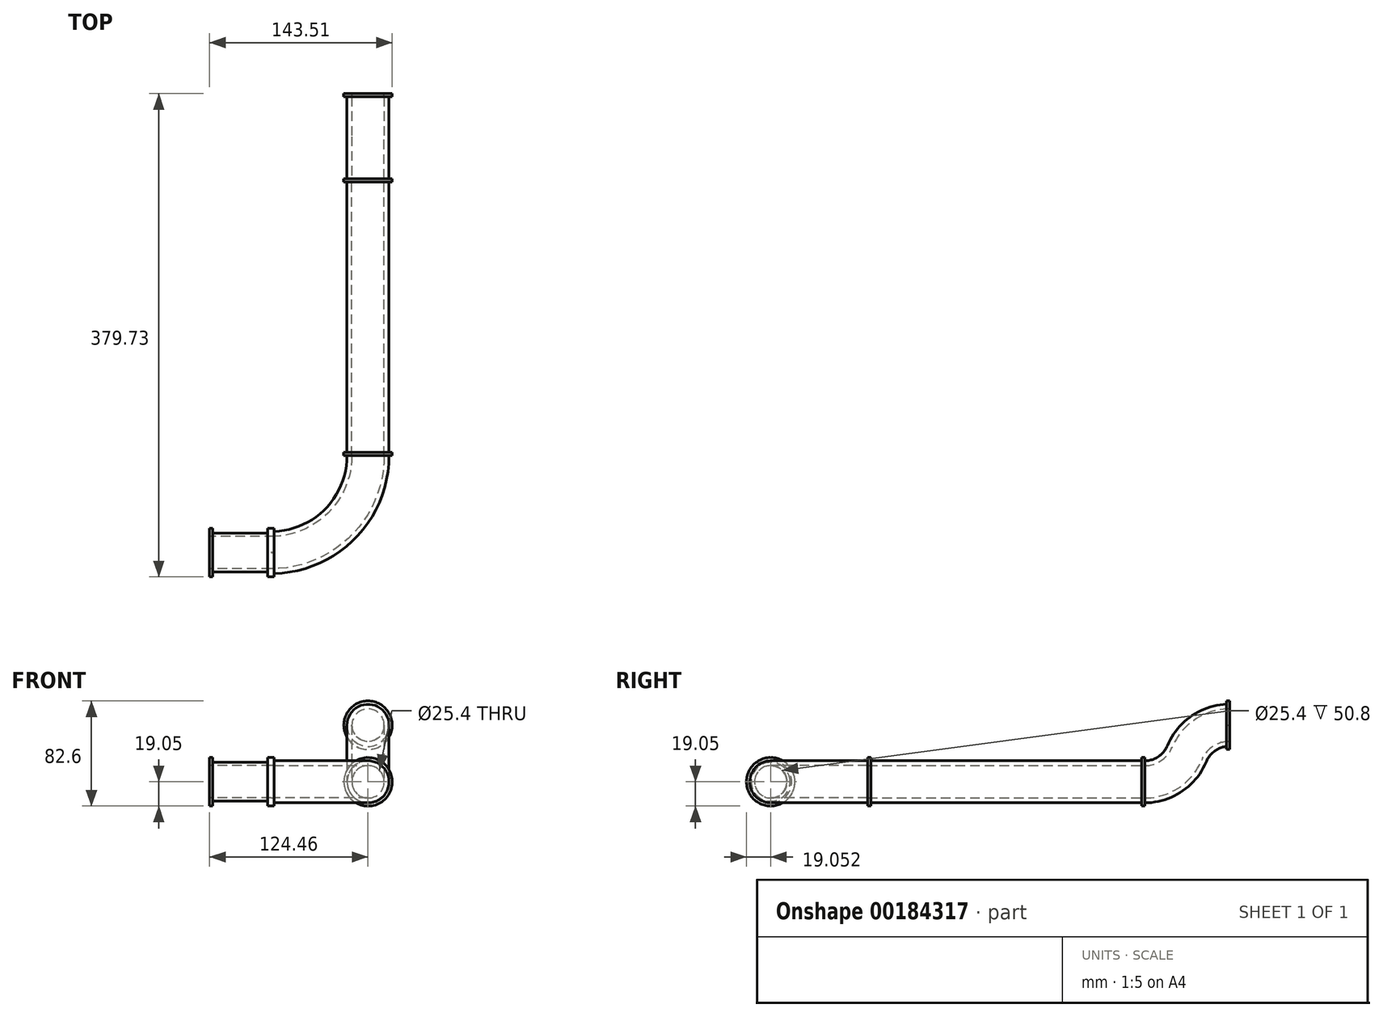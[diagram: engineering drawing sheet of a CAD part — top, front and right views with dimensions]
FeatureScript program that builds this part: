
annotation { "Feature Type Name" : "Feature", "Feature Type Description" : "" }
export const myFeature = defineFeature(function(context is Context, id is Id, definition is map)
    precondition{}
    {
        {
            var Q0;
            Q0=qCreatedBy(makeId("Front.planeOp"),FACE);
            var sketch = newSketch(context, id + "F0", { "sketchPlane" : qUnion([Q0])});
            skCircle(sketch, "E0", {"center": v(0, 0) * mm, "radius": 19.05 * mm});
            skCircle(sketch, "E1", {"center": v(0, 0) * mm, "radius": 12.7 * mm});
            skCircle(sketch, "E2", {"center": v(0, 0) * mm, "radius": 16.51 * mm});
            skSolve(sketch);
        }
        {
            var Q0;
            Q0=makeQuery(id+"F0.imprint","IMPRINT",FACE,{"disambiguationData":[TD([[makeQuery(id+"F0.imprint","IMPRINT",EDGE,{"derivedFrom":sQuery(id+"F0.wireOp",EDGE,"E0")}),1.0]])]});
            extrude(context, id + "F1", {"entities" : qUnion([Q0]), "depth" : 2.54 * mm});
        }
        {
            var Q0;
            Q0=makeQuery(id+"F0.imprint","IMPRINT",FACE,{"disambiguationData":[TD([[makeQuery(id+"F0.imprint","IMPRINT",EDGE,{"derivedFrom":sQuery(id+"F0.wireOp",EDGE,"E1")}),-1.0]])]});
            extrude(context, id + "F2", {"entities" : qUnion([Q0]), "operationType" : NewBodyOperationType.ADD, "depth" : 217.68 * mm});
        }
        {
            var Q0;
            Q0=makeQuery(id+"F2.opExtrude","CAP_FACE",FACE,{"disambiguationData":[OSD([sQuery(id+"F0.wireOp",EDGE,"E1"),sQuery(id+"F0.wireOp",EDGE,"E2")])],"isStart":false});
            var sketch = newSketch(context, id + "F3", { "sketchPlane" : qUnion([Q0])});
            skCircle(sketch, "E3", {"center": v(0, 0) * mm, "radius": 12.7 * mm});
            skCircle(sketch, "E4", {"center": v(0, 0) * mm, "radius": 19.05 * mm});
            skSolve(sketch);
        }
        {
            var Q0;
            Q0=makeQuery(id+"F3.imprint","IMPRINT",FACE,{"disambiguationData":[TD([[makeQuery(id+"F3.imprint","IMPRINT",EDGE,{"derivedFrom":sQuery(id+"F3.wireOp",EDGE,"E4")}),1.0]])]});
            extrude(context, id + "F4", {"entities" : qUnion([Q0]), "operationType" : NewBodyOperationType.ADD, "oppositeDirection" : true, "depth" : 2.54 * mm});
        }
        {
            var Q0;
            Q0=qCreatedBy(makeId("Right.planeOp"),FACE);
            var sketch = newSketch(context, id + "F5", { "sketchPlane" : qUnion([Q0])});
            skArc(sketch, "E5", {"start": v(0, 0) * mm, "mid": v(19.84, 6) * mm, "end": v(33.02, 22) * mm});
            skArc(sketch, "E6", {"start": v(66.8, 44.5) * mm, "mid": v(46.5, 38.35) * mm, "end": v(33.02, 22) * mm});
            skLineSegment(sketch, "E7", {"start": v(66.8, 44.5) * mm, "end": v(9.22, 44.5) * mm, "construction": true});
            skLineSegment(sketch, "E8", {"start": v(0, 0) * mm, "end": v(35.8, 0) * mm, "construction": true});
            skLineSegment(sketch, "E9", {"start": v(33.02, 22) * mm, "end": v(33.02, 44.5) * mm, "construction": true});
            skLineSegment(sketch, "E10", {"start": v(33.02, 44.5) * mm, "end": v(33.02, 0) * mm, "construction": true});
            skLineSegment(sketch, "E11", {"start": v(0, 0) * mm, "end": v(66.8, 44.5) * mm, "construction": true});
            skSolve(sketch);
        }
        {
            var Q0;
            Q0=makeQuery(id+"F0.imprint","IMPRINT",FACE,{"disambiguationData":[TD([[makeQuery(id+"F0.imprint","IMPRINT",EDGE,{"derivedFrom":sQuery(id+"F0.wireOp",EDGE,"E1")}),-1.0]])]});
            var Q1;
            Q1=sQuery(id+"F5.wireOp",EDGE,"E5");
            var Q2;
            Q2=sQuery(id+"F5.wireOp",EDGE,"E6");
            sweep(context, id + "F6", {"operationType" : NewBodyOperationType.ADD, "profiles" : qUnion([Q0]), "path" : qUnion([Q1, Q2])});
        }
        {
            var Q0;
            Q0=makeQuery(id+"F6.opSweep","CAP_FACE",FACE,{"disambiguationData":[OSD([sQuery(id+"F0.wireOp",EDGE,"E1"),sQuery(id+"F0.wireOp",EDGE,"E2"),sQuery(id+"F5.wireOp",VERTEX,"E6.start")])],"isStart":false});
            var sketch = newSketch(context, id + "F7", { "sketchPlane" : qUnion([Q0])});
            skCircle(sketch, "E12", {"center": v(0, 44.5) * mm, "radius": 19.05 * mm});
            skCircle(sketch, "E13", {"center": v(0, 44.5) * mm, "radius": 12.7 * mm});
            skSolve(sketch);
        }
        {
            var Q0;
            Q0 = qSketchRegion(id + "F7", true);
            extrude(context, id + "F8", {"entities" : qUnion([Q0]), "operationType" : NewBodyOperationType.ADD, "oppositeDirection" : true, "depth" : 2.54 * mm});
        }
        {
            var Q0;
            Q0=qCreatedBy(makeId("Top.planeOp"),FACE);
            var sketch = newSketch(context, id + "F9", { "sketchPlane" : qUnion([Q0])});
            skArc(sketch, "E14", {"start": v(-76.2, -293.88) * mm, "mid": v(-22.32, -271.56) * mm, "end": v(0, -217.68) * mm});
            skPoint(sketch, "E15.endSnap0", {"position": v(-22.32, -271.56) * mm});
            skSolve(sketch);
        }
        {
            var Q0;
            Q0=makeQuery(id+"F3.imprint","IMPRINT",FACE,{"disambiguationData":[TD([[makeQuery(id+"F3.imprint","IMPRINT",EDGE,{"derivedFrom":sQuery(id+"F3.wireOp",EDGE,"E3")}),-1.0]])]});
            var Q1;
            Q1=sQuery(id+"F9.wireOp",EDGE,"E14");
            sweep(context, id + "F10", {"operationType" : NewBodyOperationType.ADD, "profiles" : qUnion([Q0]), "path" : qUnion([Q1])});
        }
        {
            var Q0;
            Q0=makeQuery(id+"F10.opSweep","CAP_FACE",FACE,{"disambiguationData":[OSD([sQuery(id+"F0.wireOp",EDGE,"E2"),sQuery(id+"F3.wireOp",EDGE,"E3"),sQuery(id+"F9.wireOp",VERTEX,"E14.start")])],"isStart":false});
            var sketch = newSketch(context, id + "F11", { "sketchPlane" : qUnion([Q0])});
            skCircle(sketch, "E16", {"center": v(293.88, 0) * mm, "radius": 12.7 * mm});
            skCircle(sketch, "E17", {"center": v(293.88, 0) * mm, "radius": 19.05 * mm});
            skSolve(sketch);
        }
        {
            var Q0;
            Q0 = qSketchRegion(id + "F11", true);
            extrude(context, id + "F12", {"entities" : qUnion([Q0]), "operationType" : NewBodyOperationType.ADD, "oppositeDirection" : true, "depth" : 2.54 * mm});
        }
        {
            var Q0;
            Q0=makeQuery(id+"F12.boolean.opBoolean","MERGE",FACE,{"derivedFrom":[makeQuery(id+"F10.opSweep","CAP_FACE",FACE,{"disambiguationData":[OSD([sQuery(id+"F0.wireOp",EDGE,"E2"),sQuery(id+"F3.wireOp",EDGE,"E3"),sQuery(id+"F9.wireOp",VERTEX,"E14.start")])],"isStart":false}),makeQuery(id+"F12.opExtrude","CAP_FACE",FACE,{"disambiguationData":[OSD([sQuery(id+"F11.wireOp",EDGE,"E16"),sQuery(id+"F11.wireOp",EDGE,"E17")])],"isStart":true})]});
            var sketch = newSketch(context, id + "F13", { "sketchPlane" : qUnion([Q0])});
            skCircle(sketch, "E18", {"center": v(293.88, 0) * mm, "radius": 12.7 * mm});
            skCircle(sketch, "E19", {"center": v(293.88, 0) * mm, "radius": 19.05 * mm});
            skSolve(sketch);
        }
        {
            var Q0;
            Q0 = qSketchRegion(id + "F13", true);
            extrude(context, id + "F14", {"entities" : qUnion([Q0]), "operationType" : NewBodyOperationType.ADD, "depth" : 2.54 * mm});
        }
        {
            var Q0;
            Q0=makeQuery(id+"F14.opExtrude","CAP_FACE",FACE,{"disambiguationData":[OSD([sQuery(id+"F13.wireOp",EDGE,"E18"),sQuery(id+"F13.wireOp",EDGE,"E19")])],"isStart":false});
            var sketch = newSketch(context, id + "F15", { "sketchPlane" : qUnion([Q0])});
            skCircle(sketch, "E20", {"center": v(293.88, 0) * mm, "radius": 12.7 * mm});
            skCircle(sketch, "E21", {"center": v(293.88, 0) * mm, "radius": 15.24 * mm});
            skSolve(sketch);
        }
        {
            var Q0;
            Q0 = qSketchRegion(id + "F15", true);
            extrude(context, id + "F16", {"entities" : qUnion([Q0]), "operationType" : NewBodyOperationType.ADD, "depth" : 45.72 * mm});
        }
        {
            var Q0;
            Q0=makeQuery(id+"F16.opExtrude","CAP_FACE",FACE,{"disambiguationData":[OSD([sQuery(id+"F15.wireOp",EDGE,"E20"),sQuery(id+"F15.wireOp",EDGE,"E21")])],"isStart":false});
            var sketch = newSketch(context, id + "F17", { "sketchPlane" : qUnion([Q0])});
            skCircle(sketch, "E22", {"center": v(293.88, 0) * mm, "radius": 12.7 * mm});
            skCircle(sketch, "E23", {"center": v(293.88, 0) * mm, "radius": 19.05 * mm});
            skSolve(sketch);
        }
        {
            var Q0;
            Q0 = qSketchRegion(id + "F17", true);
            extrude(context, id + "F18", {"entities" : qUnion([Q0]), "operationType" : NewBodyOperationType.ADD, "oppositeDirection" : true, "depth" : 2.54 * mm});
        }
    });
